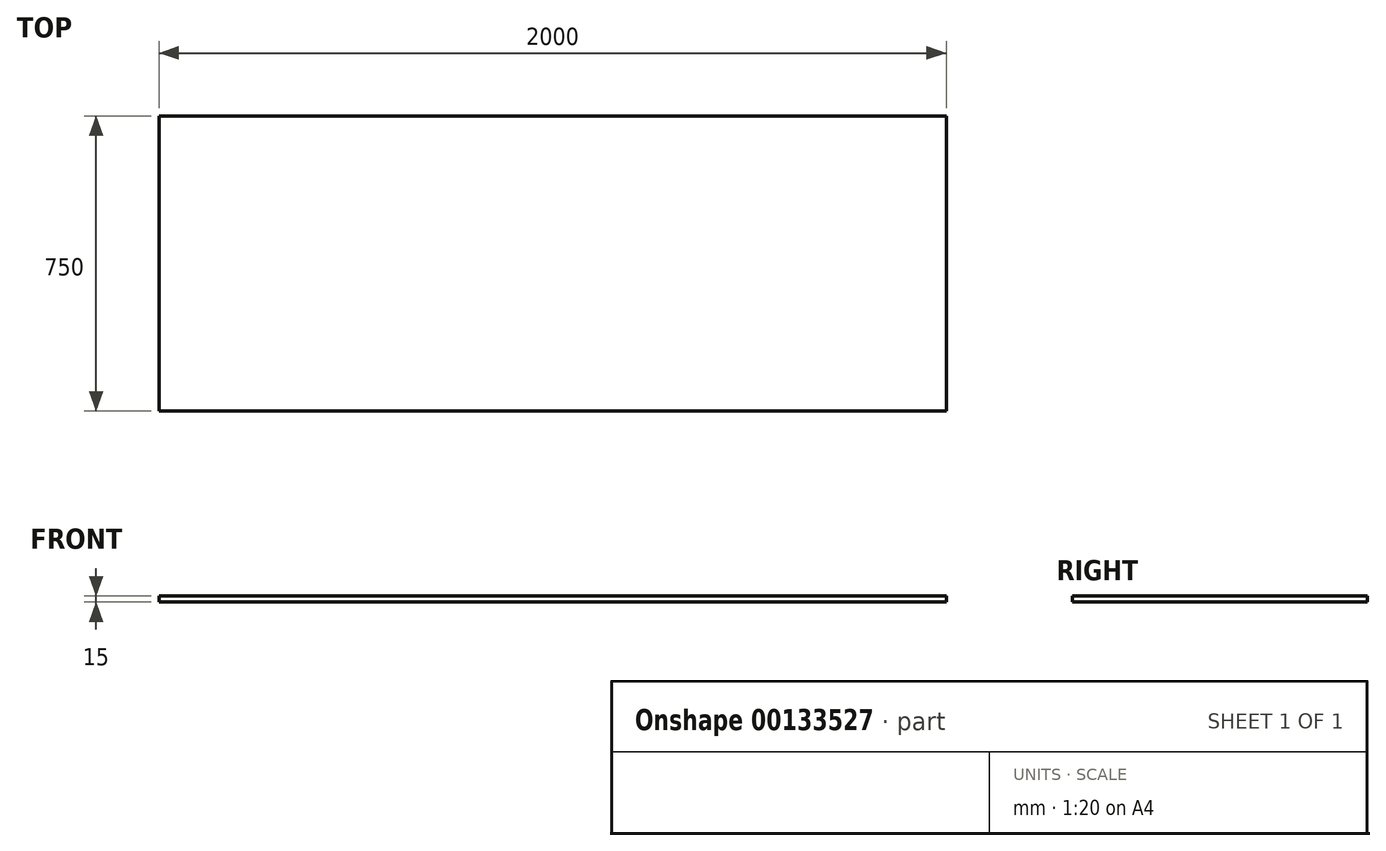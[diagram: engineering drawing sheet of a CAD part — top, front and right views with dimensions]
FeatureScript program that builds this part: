
annotation { "Feature Type Name" : "Feature", "Feature Type Description" : "" }
export const myFeature = defineFeature(function(context is Context, id is Id, definition is map)
    precondition{}
    {
        {
            var Q0;
            Q0=qCreatedBy(makeId("Right.planeOp"),FACE);
            var sketch = newSketch(context, id + "F0", { "sketchPlane" : qUnion([Q0])});
            skLineSegment(sketch, "E0.bottom", {"start": v(-375, -7.5) * mm, "end": v(375, -7.5) * mm});
            skLineSegment(sketch, "E0.top", {"start": v(-375, 7.5) * mm, "end": v(375, 7.5) * mm});
            skLineSegment(sketch, "E0.left", {"start": v(-375, -7.5) * mm, "end": v(-375, 7.5) * mm});
            skLineSegment(sketch, "E0.right", {"start": v(375, -7.5) * mm, "end": v(375, 7.5) * mm});
            skPoint(sketch, "E0.middle", {"position": v(0, 0) * mm});
            skSolve(sketch);
        }
        {
            var Q0;
            Q0=makeQuery(id+"F0.imprint","IMPRINT",FACE,{"disambiguationData":[TD([[makeQuery(id+"F0.imprint","IMPRINT",EDGE,{"derivedFrom":sQuery(id+"F0.wireOp",EDGE,"E0.bottom")}),1.0]])]});
            extrude(context, id + "F1", {"entities" : qUnion([Q0]), "endBound" : BoundingType.SYMMETRIC, "depth" : 2000 * mm});
        }
    });
